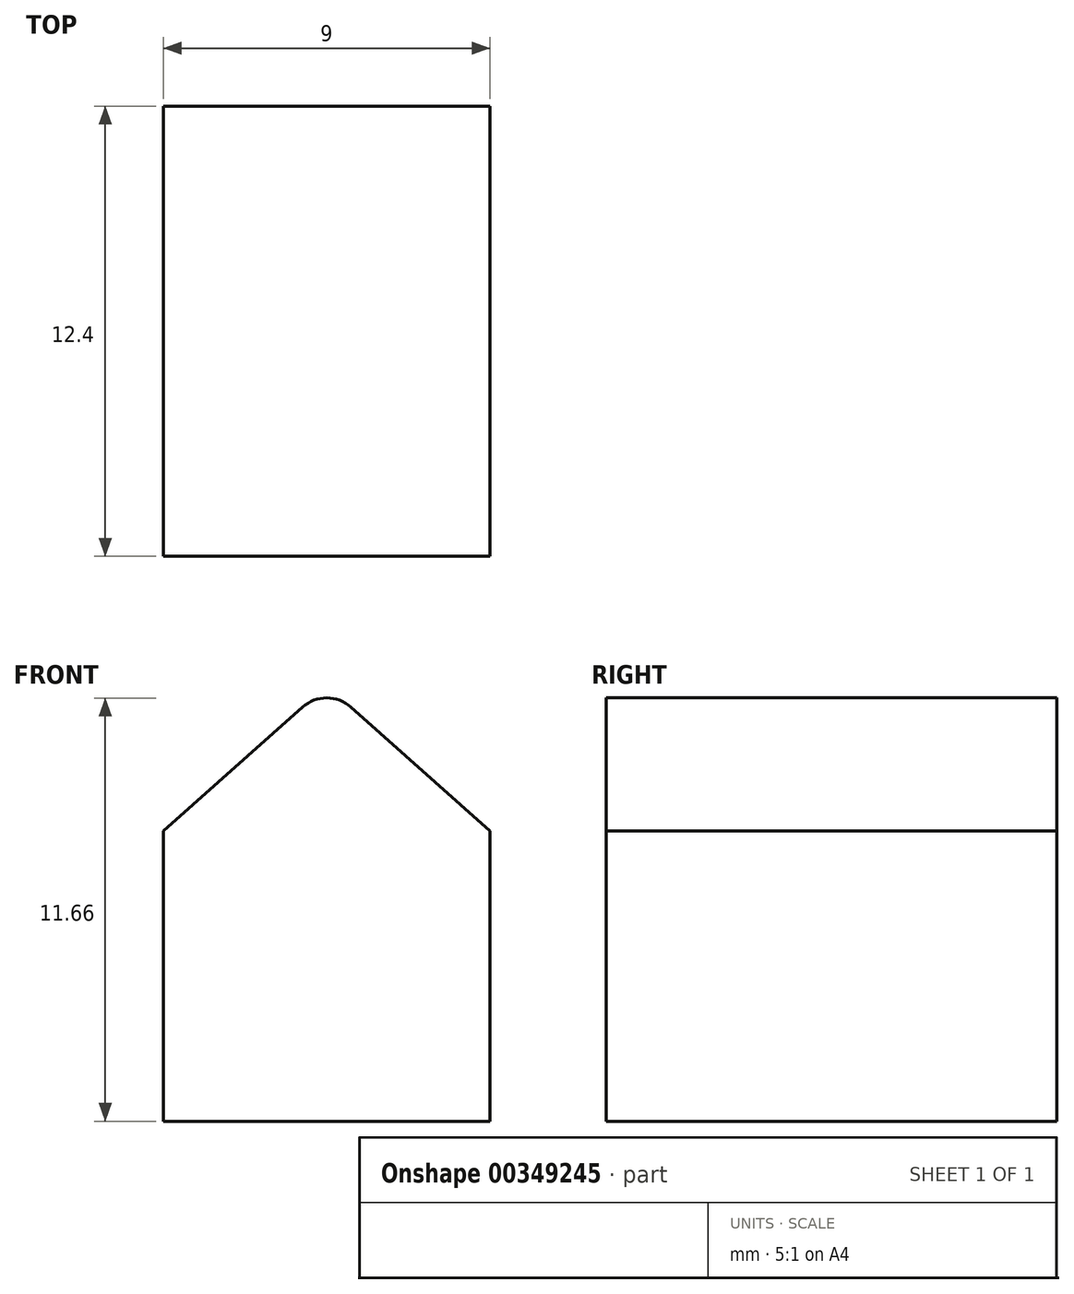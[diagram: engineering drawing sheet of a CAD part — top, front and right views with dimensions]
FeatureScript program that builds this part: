
annotation { "Feature Type Name" : "Feature", "Feature Type Description" : "" }
export const myFeature = defineFeature(function(context is Context, id is Id, definition is map)
    precondition{}
    {
        {
            var Q0;
            Q0=qCreatedBy(makeId("Top.planeOp"),FACE);
            var sketch = newSketch(context, id + "F0", { "sketchPlane" : qUnion([Q0])});
            skLineSegment(sketch, "E0.bottom", {"start": v(0, 0) * mm, "end": v(-9, 0) * mm});
            skLineSegment(sketch, "E0.top", {"start": v(0, -12.4) * mm, "end": v(-9, -12.4) * mm});
            skLineSegment(sketch, "E0.left", {"start": v(0, 0) * mm, "end": v(0, -12.4) * mm});
            skLineSegment(sketch, "E0.right", {"start": v(-9, 0) * mm, "end": v(-9, -12.4) * mm});
            skSolve(sketch);
        }
        {
            var Q0;
            Q0=qSketchRegion(id+"F0",true);
            extrude(context, id + "F1", {"entities" : qUnion([Q0]), "depth" : 4 * mm});
        }
        {
            var Q0;
            Q0=makeQuery(id+"F1.opExtrude","CAP_FACE",FACE,{"disambiguationData":[OSD([sQuery(id+"F0.wireOp",EDGE,"E0.bottom"),sQuery(id+"F0.wireOp",EDGE,"E0.top"),sQuery(id+"F0.wireOp",EDGE,"E0.left"),sQuery(id+"F0.wireOp",EDGE,"E0.right")])],"isStart":false});
            var sketch = newSketch(context, id + "F2", { "sketchPlane" : qUnion([Q0])});
            skLineSegment(sketch, "E1.bottom", {"start": v(0, -12.4) * mm, "end": v(-9, -12.4) * mm});
            skLineSegment(sketch, "E1.top", {"start": v(0, 0) * mm, "end": v(-9, 0) * mm});
            skLineSegment(sketch, "E1.left", {"start": v(0, -12.4) * mm, "end": v(0, 0) * mm});
            skLineSegment(sketch, "E1.right", {"start": v(-9, -12.4) * mm, "end": v(-9, 0) * mm});
            skSolve(sketch);
        }
        {
            var Q0;
            Q0=makeQuery(id+"F2.imprint","IMPRINT",FACE,{"disambiguationData":[TD([[makeQuery(id+"F2.imprint","IMPRINT",EDGE,{"derivedFrom":sQuery(id+"F2.wireOp",EDGE,"E1.bottom")}),-1.0]])]});
            extrude(context, id + "F3", {"entities" : qUnion([Q0]), "operationType" : NewBodyOperationType.ADD, "depth" : 4 * mm});
        }
        {
            var Q0;
            Q0=makeQuery(id+"F3.boolean.opBoolean","MERGE",FACE,{"derivedFrom":[makeQuery(id+"F1.opExtrude","SWEPT_FACE",FACE,{"disambiguationData":[OSD([sQuery(id+"F0.wireOp",EDGE,"E0.top")])]}),makeQuery(id+"F3.opExtrude","SWEPT_FACE",FACE,{"disambiguationData":[OSD([sQuery(id+"F2.wireOp",EDGE,"E1.bottom")])]})]});
            var sketch = newSketch(context, id + "F4", { "sketchPlane" : qUnion([Q0])});
            skLineSegment(sketch, "E2", {"start": v(-4.5, 8) * mm, "end": v(-4.5, 12) * mm, "construction": true});
            skLineSegment(sketch, "E3", {"start": v(-9, 8) * mm, "end": v(-4.5, 12) * mm});
            skLineSegment(sketch, "E4", {"start": v(0, 8) * mm, "end": v(-4.5, 12) * mm});
            skLineSegment(sketch, "E5", {"start": v(-9, 8) * mm, "end": v(0, 8) * mm});
            skSolve(sketch);
        }
        {
            var Q0;
            Q0=qSketchRegion(id+"F4",true);
            var Q1;
            Q1=makeQuery(id+"F3.boolean.opBoolean","MERGE",FACE,{"derivedFrom":[makeQuery(id+"F1.opExtrude","SWEPT_FACE",FACE,{"disambiguationData":[OSD([sQuery(id+"F0.wireOp",EDGE,"E0.bottom")])]}),makeQuery(id+"F3.opExtrude","SWEPT_FACE",FACE,{"disambiguationData":[OSD([sQuery(id+"F2.wireOp",EDGE,"E1.top")])]})]});
            extrude(context, id + "F5", {"entities" : qUnion([Q0]), "operationType" : NewBodyOperationType.ADD, "endBound" : BoundingType.UP_TO_SURFACE, "oppositeDirection" : true, "endBoundEntityFace" : qUnion([Q1]), "depth" : 25 * mm});
        }
        {
            var Q0;
            Q0=makeQuery(id+"F5.opExtrude","SWEPT_EDGE",EDGE,{"disambiguationData":[OSD([sQuery(id+"F4.wireOp",EDGE,"E3"),sQuery(id+"F4.wireOp",EDGE,"E4")])]});
            var Q1;
            Q1=makeQuery(id+"F3.opExtrude","CAP_EDGE",EDGE,{"disambiguationData":[OSD([sQuery(id+"F2.wireOp",EDGE,"E1.right")])],"isStart":true});
            fillet(context, id + "F6", {"entities" : qUnion([Q0, Q1]), "radius" : 1 * mm, "tangentPropagation" : true, "allowEdgeOverflow" : false});
        }
    });
